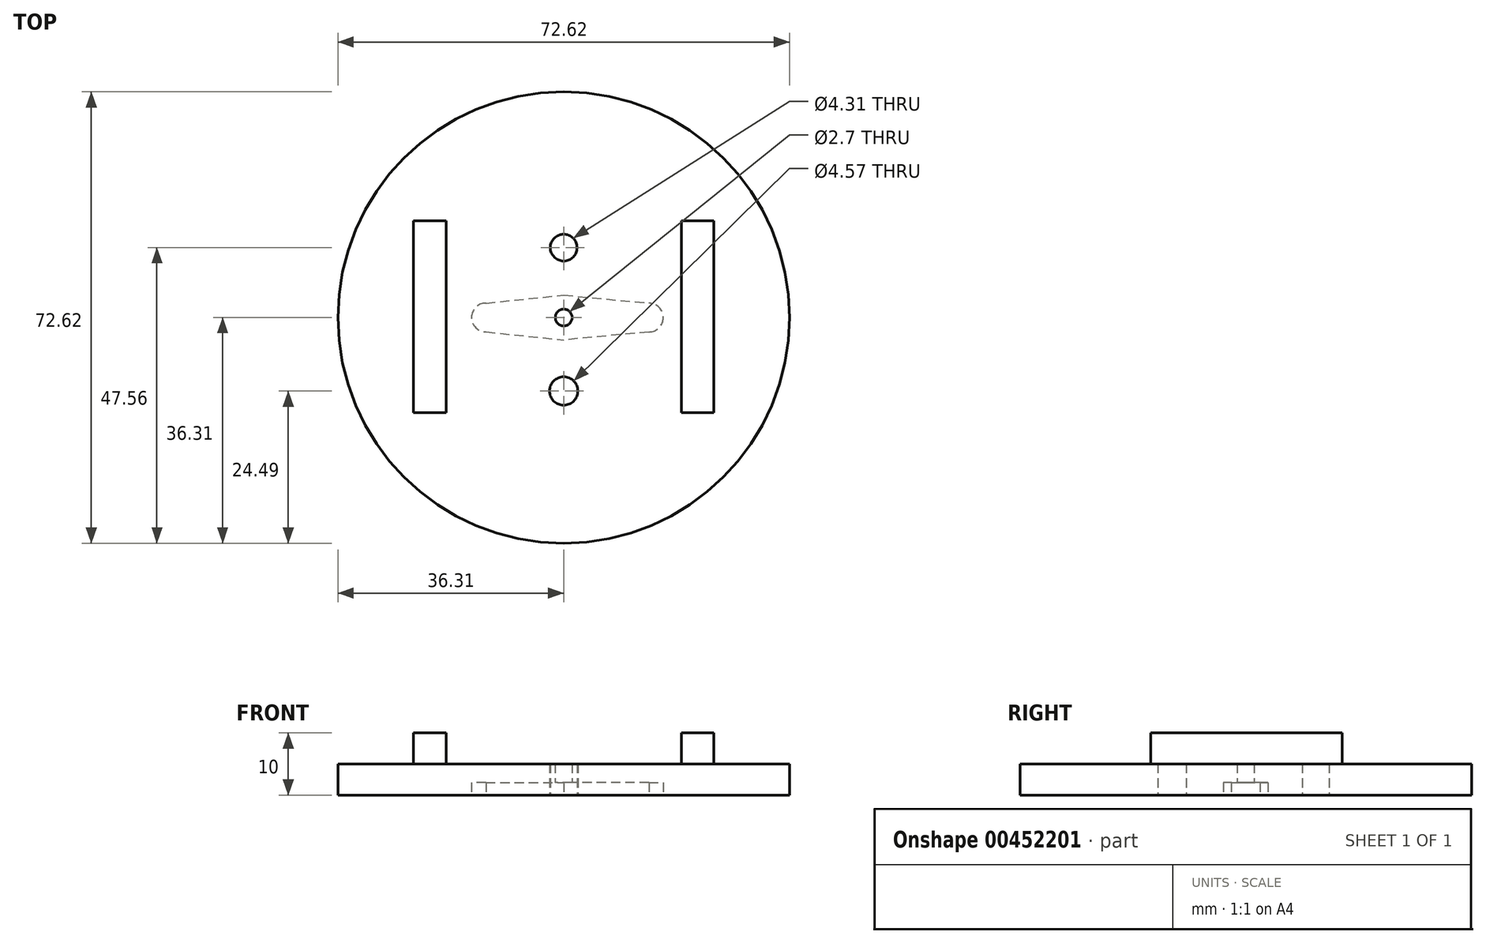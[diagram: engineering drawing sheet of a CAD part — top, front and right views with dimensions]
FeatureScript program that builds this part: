
annotation { "Feature Type Name" : "Feature", "Feature Type Description" : "" }
export const myFeature = defineFeature(function(context is Context, id is Id, definition is map)
    precondition{}
    {
        {
            var Q0;
            Q0=qCreatedBy(makeId("Top.planeOp"),FACE);
            var sketch = newSketch(context, id + "F0", { "sketchPlane" : qUnion([Q0])});
            skCircle(sketch, "E0", {"center": v(0, 0) * mm, "radius": 36.31 * mm});
            skPoint(sketch, "E1.orphan", {"position": v(-36.31, 0) * mm});
            skSolve(sketch);
        }
        {
            var Q0;
            Q0=qCreatedBy(makeId("Top.planeOp"),FACE);
            var sketch = newSketch(context, id + "F1", { "sketchPlane" : qUnion([Q0])});
            skLineSegment(sketch, "E2", {"start": v(-24.17, 0) * mm, "end": v(-24.17, 15.53) * mm});
            skLineSegment(sketch, "E3", {"start": v(-24.17, 15.53) * mm, "end": v(-24.17, -15.28) * mm});
            skLineSegment(sketch, "E4", {"start": v(-24.17, -15.28) * mm, "end": v(-18.93, -15.28) * mm});
            skLineSegment(sketch, "E5", {"start": v(-18.93, -15.28) * mm, "end": v(-18.93, 15.53) * mm});
            skLineSegment(sketch, "E6", {"start": v(-18.93, 15.53) * mm, "end": v(-24.17, 15.53) * mm});
            skPoint(sketch, "E7.start.orphan", {"position": v(-36.25, 0) * mm});
            skLineSegment(sketch, "E8.MirrorCS", {"start": v(18.93, -15.28) * mm, "end": v(18.93, 15.53) * mm});
            skLineSegment(sketch, "E9.MirrorCS", {"start": v(18.93, 15.53) * mm, "end": v(24.17, 15.53) * mm});
            skLineSegment(sketch, "E10.MirrorCS", {"start": v(24.17, 15.53) * mm, "end": v(24.17, -15.28) * mm});
            skLineSegment(sketch, "E11.MirrorCS", {"start": v(24.17, -15.28) * mm, "end": v(18.93, -15.28) * mm});
            skSolve(sketch);
        }
        {
            var Q0;
            Q0=qCreatedBy(makeId("Top.planeOp"),FACE);
            var sketch = newSketch(context, id + "F2", { "sketchPlane" : qUnion([Q0])});
            skCircle(sketch, "E12", {"center": v(0, 0) * mm, "radius": 1.35 * mm});
            skCircle(sketch, "E13", {"center": v(0, 11.25) * mm, "radius": 2.15 * mm});
            skCircle(sketch, "E14", {"center": v(0, -11.82) * mm, "radius": 2.28 * mm});
            skSolve(sketch);
        }
        {
            var Q0;
            Q0=makeQuery(id+"F0.imprint","IMPRINT",FACE,{"disambiguationData":[TD([[makeQuery(id+"F0.imprint","IMPRINT",EDGE,{"derivedFrom":sQuery(id+"F0.wireOp",EDGE,"E0")}),1.0]])]});
            extrude(context, id + "F3", {"entities" : qUnion([Q0]), "depth" : 5 * mm});
        }
        {
            var Q0;
            Q0=makeQuery(id+"F1.imprint","IMPRINT",FACE,{"disambiguationData":[TD([[makeQuery(id+"F1.imprint","IMPRINT",EDGE,{"derivedFrom":sQuery(id+"F1.wireOp",EDGE,"E8.MirrorCS")}),-1.0]])]});
            var Q1;
            {var subQ2=sQuery(id+"F1.wireOp",EDGE,"E4");Q1=makeQuery(id+"F1.imprint","IMPRINT",FACE,{"disambiguationData":[TD([[makeQuery(id+"F1.imprint","IMPRINT",EDGE,{"derivedFrom":subQ2}),1.0]])]});}
            extrude(context, id + "F4", {"entities" : qUnion([Q0, Q1]), "operationType" : NewBodyOperationType.ADD, "depth" : 10 * mm});
        }
        {
            var Q0;
            Q0=makeQuery(id+"F2.imprint","IMPRINT",FACE,{"disambiguationData":[TD([[makeQuery(id+"F2.imprint","IMPRINT",EDGE,{"derivedFrom":sQuery(id+"F2.wireOp",EDGE,"E14")}),1.0]])]});
            var Q1;
            Q1=makeQuery(id+"F2.imprint","IMPRINT",FACE,{"disambiguationData":[TD([[makeQuery(id+"F2.imprint","IMPRINT",EDGE,{"derivedFrom":sQuery(id+"F2.wireOp",EDGE,"E12")}),1.0]])]});
            var Q2;
            Q2=makeQuery(id+"F2.imprint","IMPRINT",FACE,{"disambiguationData":[TD([[makeQuery(id+"F2.imprint","IMPRINT",EDGE,{"derivedFrom":sQuery(id+"F2.wireOp",EDGE,"E13")}),1.0]])]});
            var Q3;
            Q3=sQuery(id+"F2.wireOp",EDGE,"E14");
            var Q4;
            Q4=sQuery(id+"F2.wireOp",EDGE,"E12");
            var Q5;
            Q5=sQuery(id+"F2.wireOp",EDGE,"E13");
            extrude(context, id + "F5", {"entities" : qUnion([Q0, Q1, Q2]), "operationType" : NewBodyOperationType.REMOVE, "surfaceEntities" : qUnion([Q3, Q4, Q5]), "depth" : 25 * mm});
        }
        {
            var Q0;
            Q0=qCreatedBy(makeId("Top.planeOp"),FACE);
            var sketch = newSketch(context, id + "F6", { "sketchPlane" : qUnion([Q0])});
            skCircle(sketch, "E15", {"center": v(0, 0) * mm, "radius": 3.59 * mm});
            skCircle(sketch, "E16", {"center": v(13.71, 0) * mm, "radius": 2.32 * mm});
            skCircle(sketch, "E17", {"center": v(-12.51, 0) * mm, "radius": 2.3 * mm});
            skLineSegment(sketch, "E18", {"start": v(-12.51, 0) * mm, "end": v(-12.51, -2.3) * mm});
            skLineSegment(sketch, "E19", {"start": v(-12.51, -2.3) * mm, "end": v(-12.51, 2.3) * mm});
            skLineSegment(sketch, "E20", {"start": v(13.71, 0) * mm, "end": v(13.71, -2.32) * mm});
            skLineSegment(sketch, "E21", {"start": v(13.71, -2.32) * mm, "end": v(13.71, 2.32) * mm});
            skLineSegment(sketch, "E22", {"start": v(-12.51, -2.3) * mm, "end": v(0, -3.6) * mm});
            skLineSegment(sketch, "E23", {"start": v(-12.51, 2.3) * mm, "end": v(0, 3.6) * mm});
            skLineSegment(sketch, "E24", {"start": v(0, 3.6) * mm, "end": v(13.71, 2.32) * mm});
            skLineSegment(sketch, "E25", {"start": v(13.71, -2.32) * mm, "end": v(0, -3.6) * mm});
            skSolve(sketch);
        }
        {
            var Q0;
            {var subQ0=sQuery(id+"F6.wireOp",EDGE,"E19");var subQ4=makeQuery(id+"F6.imprint","IMPRINT",VERTEX,{"derivedFrom":subQ0});Q0=makeQuery(id+"F6.imprint","IMPRINT",FACE,{"disambiguationData":[TD([[makeQuery(id+"F6.imprint","IMPRINT",EDGE,{"disambiguationData":[TD([[subQ4,1.0]])],"derivedFrom":subQ0}),-1.0]])]});}
            var Q1;
            {var subQ0=sQuery(id+"F6.wireOp",EDGE,"E19");var subQ4=makeQuery(id+"F6.imprint","IMPRINT",VERTEX,{"derivedFrom":subQ0});Q1=makeQuery(id+"F6.imprint","IMPRINT",FACE,{"disambiguationData":[TD([[makeQuery(id+"F6.imprint","IMPRINT",EDGE,{"disambiguationData":[TD([[subQ4,1.0]])],"derivedFrom":subQ0}),1.0]])]});}
            var Q2;
            {var subQ0=sQuery(id+"F6.wireOp",EDGE,"E22");var subQ1=sQuery(id+"F6.wireOp",EDGE,"E15");var subQ2=makeQuery(id+"F6.imprint","INTERSECT",VERTEX,{"derivedFrom":[subQ1,subQ0]});Q2=makeQuery(id+"F6.imprint","IMPRINT",FACE,{"disambiguationData":[TD([[makeQuery(id+"F6.imprint","IMPRINT",EDGE,{"disambiguationData":[TD([[subQ2,1.0]])],"derivedFrom":subQ1}),-1.0]])]});}
            var Q3;
            {var subQ0=sQuery(id+"F6.wireOp",EDGE,"E15");var subQ1=makeQuery(id+"F6.imprint","INTERSECT",VERTEX,{"derivedFrom":[subQ0,sQuery(id+"F6.wireOp",EDGE,"E22")]});Q3=makeQuery(id+"F6.imprint","IMPRINT",FACE,{"disambiguationData":[TD([[makeQuery(id+"F6.imprint","IMPRINT",EDGE,{"disambiguationData":[TD([[subQ1,1.0]])],"derivedFrom":subQ0}),1.0]])]});}
            var Q4;
            {var subQ0=sQuery(id+"F6.wireOp",EDGE,"E24");Q4=makeQuery(id+"F6.imprint","IMPRINT",FACE,{"disambiguationData":[TD([[makeQuery(id+"F6.imprint","IMPRINT",EDGE,{"derivedFrom":subQ0}),-1.0]])]});}
            var Q5;
            {var subQ0=sQuery(id+"F6.wireOp",EDGE,"E21");var subQ4=makeQuery(id+"F6.imprint","IMPRINT",VERTEX,{"derivedFrom":subQ0});Q5=makeQuery(id+"F6.imprint","IMPRINT",FACE,{"disambiguationData":[TD([[makeQuery(id+"F6.imprint","IMPRINT",EDGE,{"disambiguationData":[TD([[subQ4,1.0]])],"derivedFrom":subQ0}),1.0]])]});}
            var Q6;
            {var subQ0=sQuery(id+"F6.wireOp",EDGE,"E21");var subQ4=makeQuery(id+"F6.imprint","IMPRINT",VERTEX,{"derivedFrom":subQ0});Q6=makeQuery(id+"F6.imprint","IMPRINT",FACE,{"disambiguationData":[TD([[makeQuery(id+"F6.imprint","IMPRINT",EDGE,{"disambiguationData":[TD([[subQ4,1.0]])],"derivedFrom":subQ0}),-1.0]])]});}
            extrude(context, id + "F7", {"entities" : qUnion([Q0, Q1, Q2, Q3, Q4, Q5, Q6]), "operationType" : NewBodyOperationType.REMOVE, "depth" : 2 * mm});
        }
    });
